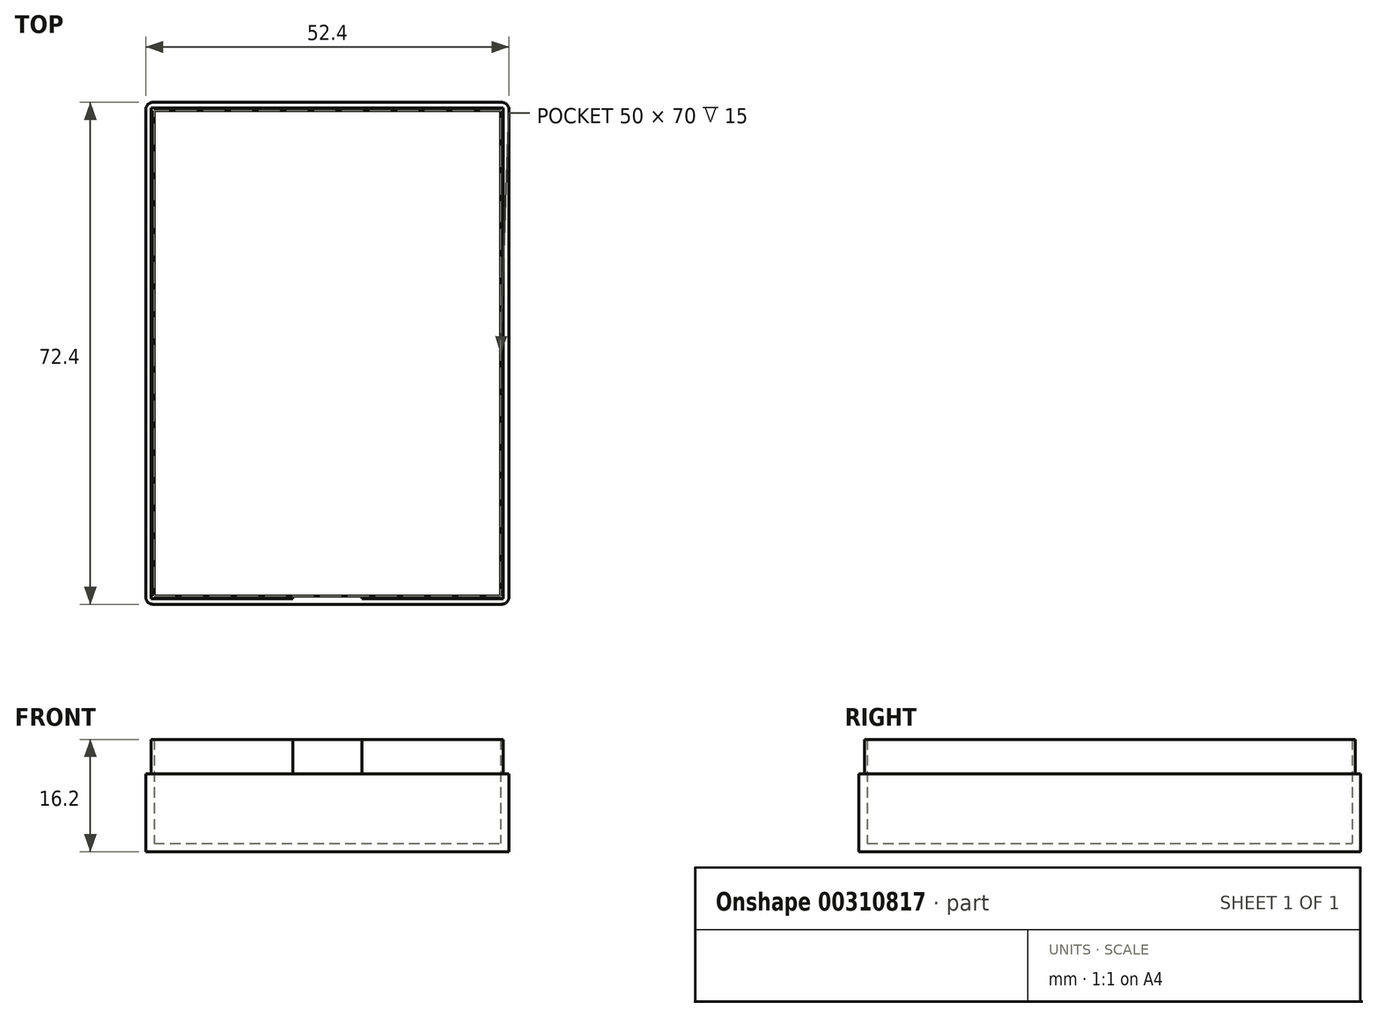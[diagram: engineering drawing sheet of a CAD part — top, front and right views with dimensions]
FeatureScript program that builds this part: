
annotation { "Feature Type Name" : "Feature", "Feature Type Description" : "" }
export const myFeature = defineFeature(function(context is Context, id is Id, definition is map)
    precondition{}
    {
        {
            var Q0;
            Q0=qCreatedBy(makeId("Top.planeOp"),FACE);
            var sketch = newSketch(context, id + "F0", { "sketchPlane" : qUnion([Q0])});
            skLineSegment(sketch, "E0.bottom", {"start": v(0, 0) * mm, "end": v(50, 0) * mm});
            skLineSegment(sketch, "E0.top", {"start": v(0, 70) * mm, "end": v(50, 70) * mm});
            skLineSegment(sketch, "E0.left", {"start": v(0, 0) * mm, "end": v(0, 70) * mm});
            skLineSegment(sketch, "E0.right", {"start": v(50, 0) * mm, "end": v(50, 70) * mm});
            skLineSegment(sketch, "E1", {"start": v(25, 70) * mm, "end": v(25, 0) * mm, "construction": true});
            skLineSegment(sketch, "E2", {"start": v(0, 35) * mm, "end": v(50, 35) * mm, "construction": true});
            skSolve(sketch);
        }
        {
            var Q0;
            Q0 = qSketchRegion(id + "F0", true);
            extrude(context, id + "F1", {"entities" : qUnion([Q0]), "depth" : 15 * mm});
        }
        {
            var Q0;
            Q0=makeQuery(id+"F1.opExtrude","CAP_FACE",FACE,{"disambiguationData":[OSD([sQuery(id+"F0.wireOp",EDGE,"E0.bottom"),sQuery(id+"F0.wireOp",EDGE,"E0.top"),sQuery(id+"F0.wireOp",EDGE,"E0.left"),sQuery(id+"F0.wireOp",EDGE,"E0.right")])],"isStart":false});
            shell(context, id + "F2", {"entities" : qUnion([Q0]), "thickness" : 1.2 * mm, "oppositeDirection" : true});
        }
        {
            var Q0;
            Q0=makeQuery(id+"F1.opExtrude","CAP_FACE",FACE,{"disambiguationData":[OSD([sQuery(id+"F0.wireOp",EDGE,"E0.bottom"),sQuery(id+"F0.wireOp",EDGE,"E0.top"),sQuery(id+"F0.wireOp",EDGE,"E0.left"),sQuery(id+"F0.wireOp",EDGE,"E0.right")])],"isStart":false});
            var sketch = newSketch(context, id + "F3", { "sketchPlane" : qUnion([Q0])});
            skLineSegment(sketch, "E3.0", {"start": v(50.4, -0.4) * mm, "end": v(50.4, 70.4) * mm});
            skLineSegment(sketch, "E3.1", {"start": v(-0.4, -0.4) * mm, "end": v(50.4, -0.4) * mm});
            skLineSegment(sketch, "E3.2", {"start": v(-0.4, -0.4) * mm, "end": v(-0.4, 70.4) * mm});
            skLineSegment(sketch, "E3.3", {"start": v(-0.4, 70.4) * mm, "end": v(50.4, 70.4) * mm});
            skLineSegment(sketch, "E4.0", {"start": v(-1.2, -1.2) * mm, "end": v(51.2, -1.2) * mm});
            skLineSegment(sketch, "E4.1", {"start": v(-1.2, -1.2) * mm, "end": v(-1.2, 71.2) * mm});
            skLineSegment(sketch, "E4.2", {"start": v(-1.2, 71.2) * mm, "end": v(51.2, 71.2) * mm});
            skLineSegment(sketch, "E4.3", {"start": v(51.2, -1.2) * mm, "end": v(51.2, 71.2) * mm});
            skSolve(sketch);
        }
        {
            var Q0;
            Q0 = qSketchRegion(id + "F3", true);
            extrude(context, id + "F4", {"entities" : qUnion([Q0]), "operationType" : NewBodyOperationType.REMOVE, "oppositeDirection" : true, "depth" : 5 * mm});
        }
        {
            var Q0;
            Q0=makeQuery(id+"F1.opExtrude","SWEPT_EDGE",EDGE,{"disambiguationData":[OSD([sQuery(id+"F0.wireOp",EDGE,"E0.bottom"),sQuery(id+"F0.wireOp",EDGE,"E0.left")])]});
            var Q1;
            Q1=makeQuery(id+"F1.opExtrude","SWEPT_EDGE",EDGE,{"disambiguationData":[OSD([sQuery(id+"F0.wireOp",EDGE,"E0.top"),sQuery(id+"F0.wireOp",EDGE,"E0.left")])]});
            var Q2;
            Q2=makeQuery(id+"F1.opExtrude","SWEPT_EDGE",EDGE,{"disambiguationData":[OSD([sQuery(id+"F0.wireOp",EDGE,"E0.top"),sQuery(id+"F0.wireOp",EDGE,"E0.right")])]});
            var Q3;
            Q3=makeQuery(id+"F1.opExtrude","SWEPT_EDGE",EDGE,{"disambiguationData":[OSD([sQuery(id+"F0.wireOp",EDGE,"E0.bottom"),sQuery(id+"F0.wireOp",EDGE,"E0.right")])]});
            fillet(context, id + "F5", {"entities" : qUnion([Q0, Q1, Q2, Q3]), "radius" : 1 * mm, "tangentPropagation" : true, "allowEdgeOverflow" : false});
        }
        {
            var Q0;
            Q0=makeQuery(id+"F1.opExtrude","SWEPT_FACE",FACE,{"disambiguationData":[OSD([sQuery(id+"F0.wireOp",EDGE,"E0.bottom")])]});
            var sketch = newSketch(context, id + "F6", { "sketchPlane" : qUnion([Q0])});
            skLineSegment(sketch, "E5.bottom", {"start": v(30, 10) * mm, "end": v(20, 10) * mm});
            skLineSegment(sketch, "E5.top", {"start": v(30, 20) * mm, "end": v(20, 20) * mm});
            skLineSegment(sketch, "E5.left", {"start": v(30, 10) * mm, "end": v(30, 20) * mm});
            skLineSegment(sketch, "E5.right", {"start": v(20, 10) * mm, "end": v(20, 20) * mm});
            skPoint(sketch, "E5.middle", {"position": v(25, 15) * mm});
            skPoint(sketch, "E5.middle.positionSnap0", {"position": v(25, 10) * mm});
            skPoint(sketch, "E5.centerSnap0", {"position": v(25, 10) * mm});
            skSolve(sketch);
        }
        {
            var Q0;
            Q0 = qSketchRegion(id + "F6", true);
            extrude(context, id + "F7", {"entities" : qUnion([Q0]), "operationType" : NewBodyOperationType.REMOVE, "oppositeDirection" : true, "depth" : 25 * mm});
        }
    });
